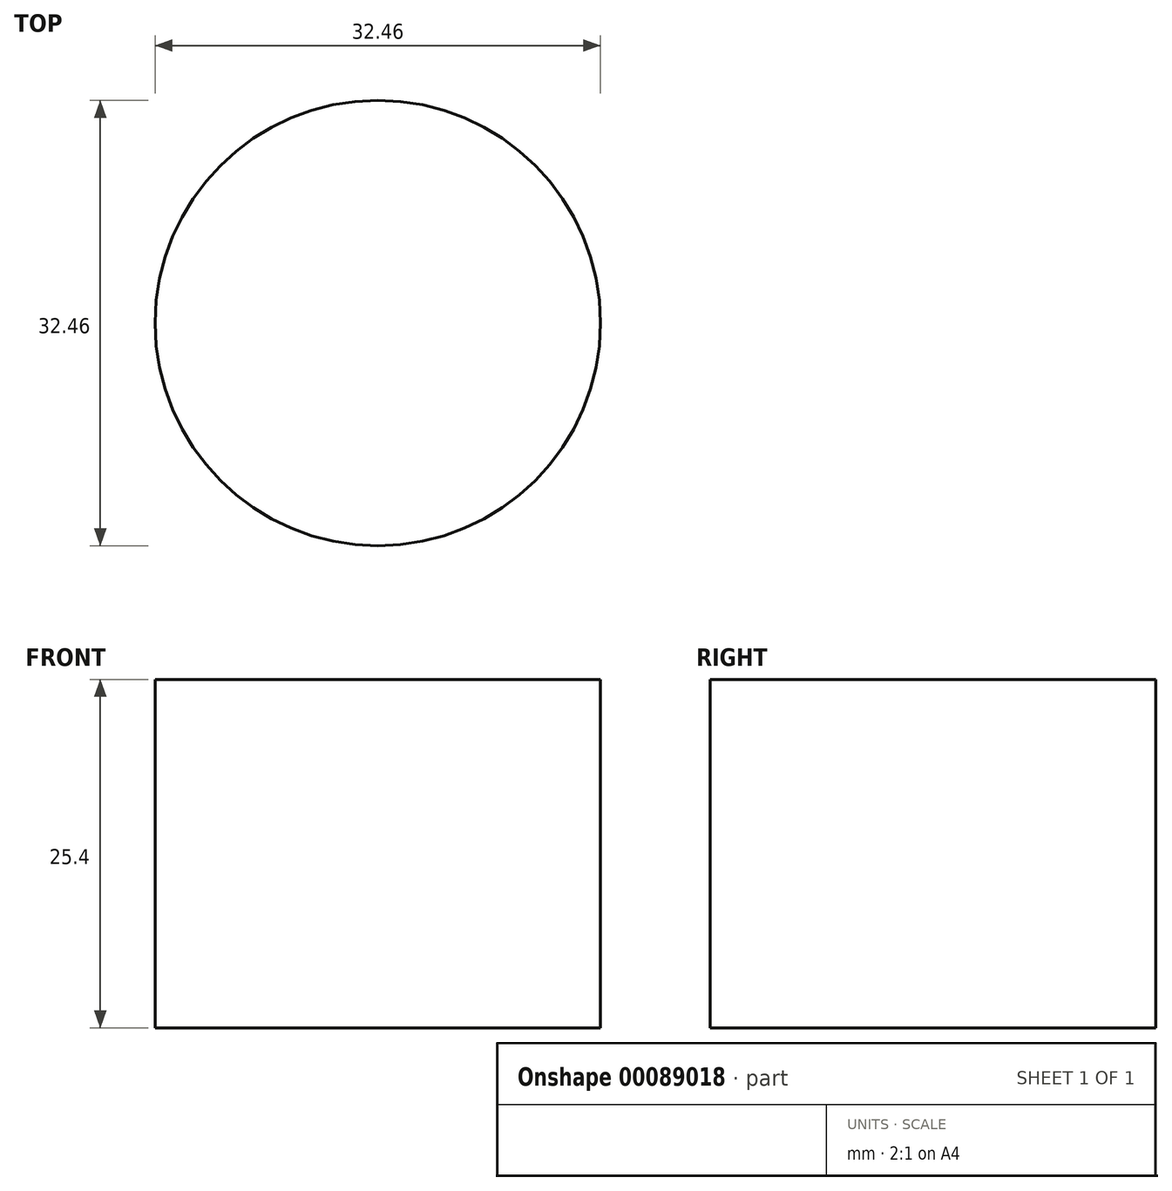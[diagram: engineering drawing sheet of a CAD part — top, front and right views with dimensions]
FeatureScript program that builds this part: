
annotation { "Feature Type Name" : "Feature", "Feature Type Description" : "" }
export const myFeature = defineFeature(function(context is Context, id is Id, definition is map)
    precondition{}
    {
        {
            var Q0;
            Q0=qCreatedBy(makeId("Top.planeOp"),FACE);
            var sketch = newSketch(context, id + "F0", { "sketchPlane" : qUnion([Q0])});
            skCircle(sketch, "E0", {"center": v(0, 0) * mm, "radius": 16.23 * mm});
            skSolve(sketch);
        }
        {
            var Q0;
            Q0 = qSketchRegion(id + "F0", true);
            extrude(context, id + "F1", {"entities" : qUnion([Q0]), "depth" : 25.4 * mm});
        }
    });
